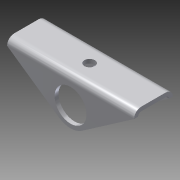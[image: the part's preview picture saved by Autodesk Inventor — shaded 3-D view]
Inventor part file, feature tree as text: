
AUTODESK INVENTOR PART (.ipt)
format: ipt  version: 2014 (Build 180170000, 170)  size: 155,648 bytes
history: native  units: in
note: dims shown in document units (in); Inventor stores cm internally (conversion verified against a paired STEP export)
features: sheet_metal_op x7, sketch x5, other x5, projected_geometry x1
ambient origin geometry x8: Origin, YZ Plane, XZ Plane, XY Plane, X Axis, Y Axis, Z Axis, Center Point
bodies: Solid1 (feature_tree)
feature tree (18):
  sheet_metal_op  "Face1"
  sheet_metal_op  "Flange1"
  sheet_metal_op  "Flange2"
  sketch  "Sketch1"  dims[d0=0.503in]
  other  "Plate1"
  sketch  "Sketch2"  dims[d1=0.3125in]
  other  "Plate2"
  sheet_metal_op  "Bend1"
  sheet_metal_op  "Corner1"
  sketch  "Sketch3"  dims[d2=1.0in]
  sketch  "Sketch4"  dims[d3=0.0625in]
  other  "Plate3"
  sheet_metal_op  "Bend2"
  sheet_metal_op  "Corner2"
  sketch  "Sketch5"  dims[d4=0.0625in d5=0.0625in d6=0.0312in d7=0.125in d8=0.0625in d9=0.5in d10=90.0deg d11=0.05in d12=0.25in d13=0.0625in d14=0.0625in d18=0.0625in d19=0.0in d35=0.164in d36=0.1875in d37=1.0in d39=0.0625in d40=0.0312in d41=0.125in d42=0.0625in d43=0.7515in d44=90.0deg d45=0.05in d46=0.25in d47=0.0625in d48=0.0625in d49=0.0625in d50=0.0in]
  projected_geometry  "Projected Loop1"
  other  "Cut1"
  other  "Cut2"
